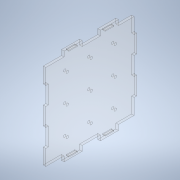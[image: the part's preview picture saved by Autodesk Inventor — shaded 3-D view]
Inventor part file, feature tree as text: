
AUTODESK INVENTOR PART (.ipt)
format: ipt  version: 2021 (Build 250183000, 183)  size: 196,096 bytes
history: native  units: mm
features: sketch x10, hole x9, extrude x1
ambient origin geometry x8: Origin, YZ Plane, XZ Plane, XY Plane, X Axis, Y Axis, Z Axis, Center Point
bodies: Solid1 (feature_tree)
feature tree (20):
  extrude  "Extrusion1"  Depth=3.0mm
  hole  "Hole2"  [1 undecoded]
  hole  "Hole3"  [1 undecoded]
  hole  "Hole4"  [1 undecoded]
  hole  "Hole5"  [1 undecoded]
  hole  "Hole6"  [1 undecoded]
  hole  "Hole7"  [1 undecoded]
  hole  "Hole8"  [1 undecoded]
  hole  "Hole9"  [1 undecoded]
  hole  "Hole10"  [1 undecoded]
  sketch  "Sketch1"  dims[d4=3.0mm d5=0.0mm d22=3.0mm]
  sketch  "Sketch3"  dims[d23=3.0mm d24=6.0mm d25=4.0mm d26=2.0mm d27=90.0deg d28=8.0mm d29=20.594885mm d30=3.0mm]
  sketch  "Sketch4"  dims[d31=3.0mm d32=6.0mm d33=4.0mm d34=2.0mm d35=90.0deg d36=8.0mm d37=20.594885mm d38=3.0mm]
  sketch  "Sketch5"  dims[d39=3.0mm d40=6.0mm d41=4.0mm d42=2.0mm d43=90.0deg d44=8.0mm d45=20.594885mm d46=3.0mm]
  sketch  "Sketch6"  dims[d47=3.0mm d48=6.0mm d49=4.0mm d50=2.0mm d51=90.0deg d52=8.0mm d53=20.594885mm d54=3.0mm]
  sketch  "Sketch7"  dims[d55=3.0mm d56=6.0mm d57=4.0mm d58=2.0mm d59=90.0deg d60=8.0mm d61=20.594885mm d62=3.0mm]
  sketch  "Sketch8"  dims[d63=3.0mm d64=6.0mm d65=4.0mm d66=2.0mm d67=90.0deg d68=8.0mm d69=20.594885mm d70=3.0mm]
  sketch  "Sketch9"  dims[d71=3.0mm d72=6.0mm d73=4.0mm d74=2.0mm d75=90.0deg d76=8.0mm d77=20.594885mm d78=3.0mm]
  sketch  "Sketch10"  dims[d79=3.0mm d80=6.0mm d81=4.0mm d82=2.0mm d83=90.0deg d84=8.0mm d85=20.594885mm d86=3.0mm]
  sketch  "Sketch11"  dims[d87=3.0mm d88=6.0mm d89=4.0mm d90=2.0mm d91=90.0deg d92=8.0mm d93=20.594885mm d94=1.0mm d95=10.0mm d96=1.0mm d97=10.0mm d98=10.0mm d99=1.0mm d100=10.0mm]
note: 9 required parameter values undecoded (feature->parameter linkage not recoverable at this tier; creation-order binding heuristic only, values carry confidence <= 0.55)
